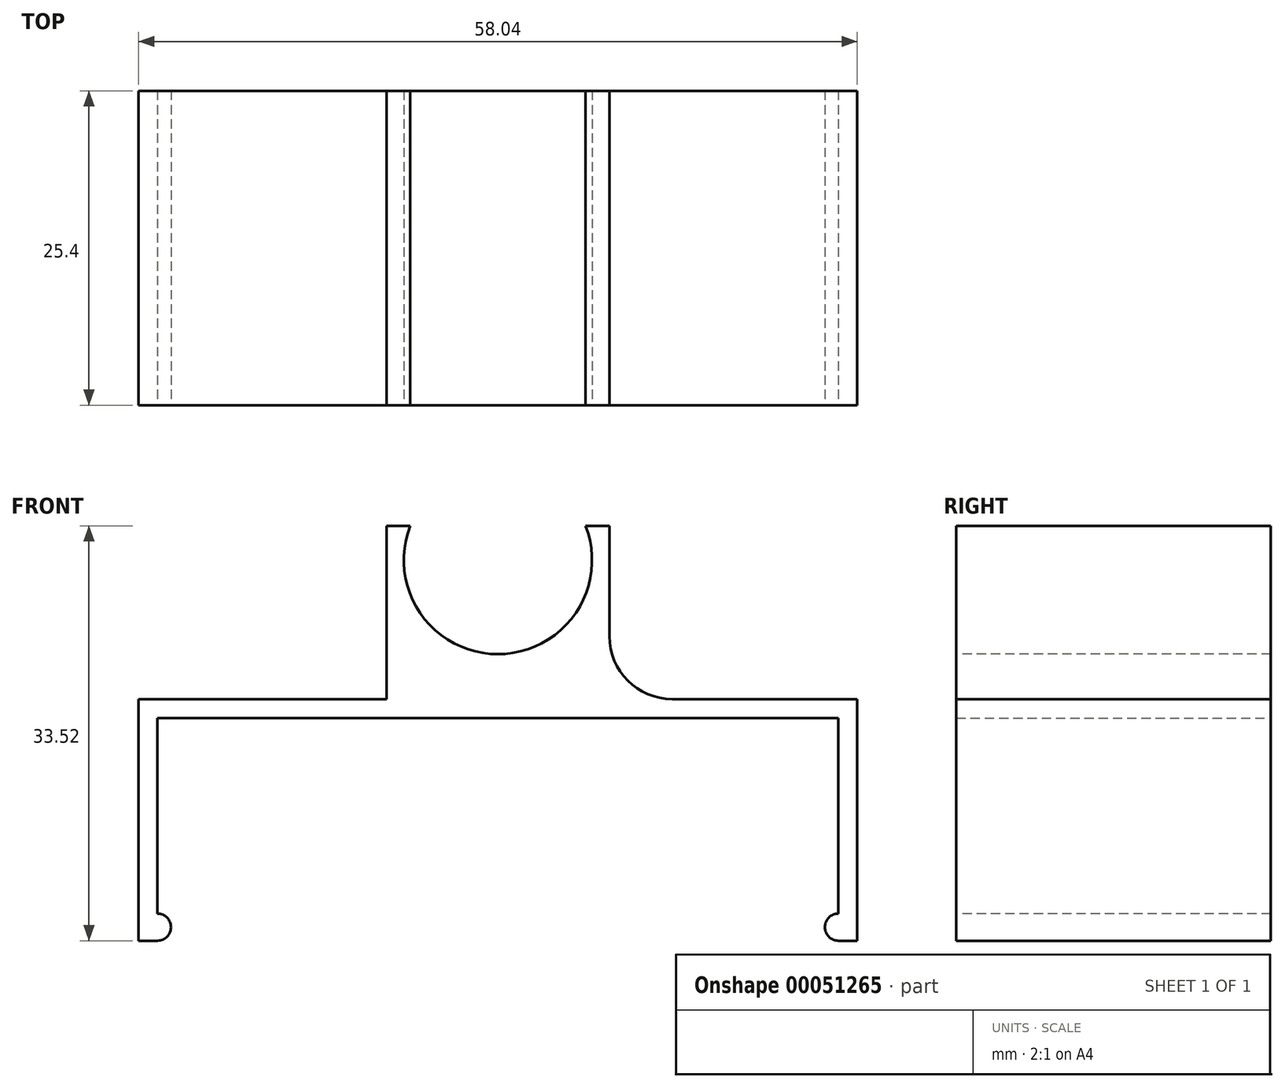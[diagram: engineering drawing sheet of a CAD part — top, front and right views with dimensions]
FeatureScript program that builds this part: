
annotation { "Feature Type Name" : "Feature", "Feature Type Description" : "" }
export const myFeature = defineFeature(function(context is Context, id is Id, definition is map)
    precondition{}
    {
        {
            var Q0;
            Q0=qCreatedBy(makeId("Front.planeOp"),FACE);
            var sketch = newSketch(context, id + "F0", { "sketchPlane" : qUnion([Q0])});
            skLineSegment(sketch, "E0", {"start": v(0, -30.9) * mm, "end": v(0, 35.03) * mm, "construction": true});
            skLineSegment(sketch, "E1", {"start": v(27.5, 0) * mm, "end": v(27.5, 18) * mm});
            skLineSegment(sketch, "E2", {"start": v(27.5, 18) * mm, "end": v(0, 18) * mm});
            skLineSegment(sketch, "E3.MirrorCS", {"start": v(-27.5, 18) * mm, "end": v(0, 18) * mm});
            skLineSegment(sketch, "E4.MirrorCS", {"start": v(-27.5, 0) * mm, "end": v(-27.5, 18) * mm});
            skLineSegment(sketch, "E5.0", {"start": v(29.02, 0) * mm, "end": v(29.02, 19.52) * mm});
            skLineSegment(sketch, "E5.1", {"start": v(29.02, 19.52) * mm, "end": v(0, 19.52) * mm});
            skLineSegment(sketch, "E5.2", {"start": v(-29.02, 19.52) * mm, "end": v(0, 19.52) * mm});
            skLineSegment(sketch, "E5.3", {"start": v(-29.02, 0) * mm, "end": v(-29.02, 19.52) * mm});
            skLineSegment(sketch, "E6", {"start": v(-29.02, 0) * mm, "end": v(-27.5, 0) * mm});
            skLineSegment(sketch, "E7", {"start": v(27.5, 0) * mm, "end": v(29.02, 0) * mm});
            skSolve(sketch);
        }
        {
            var Q0;
            Q0 = qSketchRegion(id + "F0", true);
            extrude(context, id + "F1", {"entities" : qUnion([Q0]), "endBound" : BoundingType.SYMMETRIC, "depth" : 25.4 * mm});
        }
        {
            var Q0;
            Q0=makeQuery(id+"F1.opExtrude","CAP_FACE",FACE,{"disambiguationData":[OSD([sQuery(id+"F0.wireOp",EDGE,"E1"),sQuery(id+"F0.wireOp",EDGE,"E2"),sQuery(id+"F0.wireOp",EDGE,"E3.MirrorCS"),sQuery(id+"F0.wireOp",EDGE,"E4.MirrorCS"),sQuery(id+"F0.wireOp",EDGE,"E5.0"),sQuery(id+"F0.wireOp",EDGE,"E5.1"),sQuery(id+"F0.wireOp",EDGE,"E5.2"),sQuery(id+"F0.wireOp",EDGE,"E5.3"),sQuery(id+"F0.wireOp",EDGE,"E6"),sQuery(id+"F0.wireOp",EDGE,"E7")])],"isStart":false});
            var sketch = newSketch(context, id + "F2", { "sketchPlane" : qUnion([Q0])});
            skArc(sketch, "E8", {"start": v(-27.5, 0) * mm, "mid": v(-26.4, 1.1) * mm, "end": v(-27.5, 2.2) * mm});
            skLineSegment(sketch, "E9", {"start": v(-27.5, 2.2) * mm, "end": v(-27.5, 0) * mm});
            skSolve(sketch);
        }
        {
            var Q0;
            Q0=makeQuery(id+"F2.imprint","IMPRINT",FACE,{"disambiguationData":[TD([[makeQuery(id+"F2.imprint","IMPRINT",EDGE,{"derivedFrom":sQuery(id+"F2.wireOp",EDGE,"E8")}),1.0]])]});
            var Q1;
            Q1=makeQuery(id+"F1.opExtrude","CAP_FACE",FACE,{"disambiguationData":[OSD([sQuery(id+"F0.wireOp",EDGE,"E1"),sQuery(id+"F0.wireOp",EDGE,"E2"),sQuery(id+"F0.wireOp",EDGE,"E3.MirrorCS"),sQuery(id+"F0.wireOp",EDGE,"E4.MirrorCS"),sQuery(id+"F0.wireOp",EDGE,"E5.0"),sQuery(id+"F0.wireOp",EDGE,"E5.1"),sQuery(id+"F0.wireOp",EDGE,"E5.2"),sQuery(id+"F0.wireOp",EDGE,"E5.3"),sQuery(id+"F0.wireOp",EDGE,"E6"),sQuery(id+"F0.wireOp",EDGE,"E7")])],"isStart":true});
            extrude(context, id + "F3", {"entities" : qUnion([Q0]), "endBound" : BoundingType.UP_TO_SURFACE, "oppositeDirection" : true, "endBoundEntityFace" : qUnion([Q1]), "depth" : 25.4 * mm});
        }
        {
            var Q0;
            Q0=makeQuery(id+"F3.opExtrude","SWEPT_BODY",BODY,{"disambiguationData":[OSD([sQuery(id+"F2.wireOp",EDGE,"E8"),sQuery(id+"F2.wireOp",EDGE,"E9")])]});
            var Q1;
            Q1=qCreatedBy(makeId("Right.planeOp"),FACE);
            mirror(context, id + "F4", {"operationType" : NewBodyOperationType.ADD, "entities" : qUnion([Q0]), "mirrorPlane" : qUnion([Q1])});
        }
        {
            var Q0;
            Q0=makeQuery(id+"F1.opExtrude","SWEPT_FACE",FACE,{"disambiguationData":[OSD([sQuery(id+"F0.wireOp",EDGE,"E5.1"),sQuery(id+"F0.wireOp",EDGE,"E5.2")])]});
            var sketch = newSketch(context, id + "F5", { "sketchPlane" : qUnion([Q0])});
            skLineSegment(sketch, "E10.rect.bottom", {"start": v(9, -12.7) * mm, "end": v(-9, -12.7) * mm});
            skLineSegment(sketch, "E10.rect.top", {"start": v(9, 12.7) * mm, "end": v(-9, 12.7) * mm});
            skLineSegment(sketch, "E10.rect.left", {"start": v(9, -12.7) * mm, "end": v(9, 12.7) * mm});
            skLineSegment(sketch, "E10.rect.right", {"start": v(-9, -12.7) * mm, "end": v(-9, 12.7) * mm});
            skPoint(sketch, "E10.rect.middle", {"position": v(0, 0) * mm});
            skSolve(sketch);
        }
        {
            var Q0;
            Q0=makeQuery(id+"F5.imprint","IMPRINT",FACE,{"disambiguationData":[TD([[makeQuery(id+"F5.imprint","IMPRINT",EDGE,{"derivedFrom":sQuery(id+"F5.wireOp",EDGE,"E10.rect.bottom")}),-1.0]])]});
            extrude(context, id + "F6", {"entities" : qUnion([Q0]), "operationType" : NewBodyOperationType.ADD, "depth" : 14 * mm});
        }
        {
            var Q0;
            {var subQ0=makeQuery(id+"F3.opExtrude","CAP_FACE",FACE,{"disambiguationData":[OSD([sQuery(id+"F2.wireOp",EDGE,"E8"),sQuery(id+"F2.wireOp",EDGE,"E9")])],"isStart":true});Q0=makeQuery(id+"F6.boolean.opBoolean","MERGE",FACE,{"derivedFrom":[makeQuery(id+"F4.boolean.opBoolean","MERGE",FACE,{"derivedFrom":[makeQuery(id+"F1.opExtrude","CAP_FACE",FACE,{"disambiguationData":[OSD([sQuery(id+"F0.wireOp",EDGE,"E1"),sQuery(id+"F0.wireOp",EDGE,"E2"),sQuery(id+"F0.wireOp",EDGE,"E3.MirrorCS"),sQuery(id+"F0.wireOp",EDGE,"E4.MirrorCS"),sQuery(id+"F0.wireOp",EDGE,"E5.0"),sQuery(id+"F0.wireOp",EDGE,"E5.1"),sQuery(id+"F0.wireOp",EDGE,"E5.2"),sQuery(id+"F0.wireOp",EDGE,"E5.3"),sQuery(id+"F0.wireOp",EDGE,"E6"),sQuery(id+"F0.wireOp",EDGE,"E7")])],"isStart":false}),subQ0,makeQuery(id+"F4.opPattern","COPY",FACE,{"derivedFrom":subQ0,"instanceName":"1"})]}),makeQuery(id+"F6.opExtrude","SWEPT_FACE",FACE,{"disambiguationData":[OSD([sQuery(id+"F5.wireOp",EDGE,"E10.rect.bottom")])]})]});}
            var sketch = newSketch(context, id + "F7", { "sketchPlane" : qUnion([Q0])});
            skCircle(sketch, "E11", {"center": v(0, 30.75) * mm, "radius": 7.6 * mm});
            skPoint(sketch, "E12", {"position": v(0, 33.52) * mm});
            skSolve(sketch);
        }
        {
            var Q0;
            {var subQ0=sQuery(id+"F7.wireOp",EDGE,"E11");var subQ1=makeQuery(id+"F6.opExtrude","CAP_EDGE",EDGE,{"disambiguationData":[OSD([sQuery(id+"F5.wireOp",EDGE,"E10.rect.bottom")])],"isStart":false});var subQ2=makeQuery(id+"F7.imprint","INTERSECT",VERTEX,{"disambiguationData":[OD(0.0)],"derivedFrom":[subQ1,subQ0]});Q0=makeQuery(id+"F7.imprint","IMPRINT",FACE,{"disambiguationData":[TD([[makeQuery(id+"F7.imprint","IMPRINT",EDGE,{"disambiguationData":[TD([[subQ2,1.0]])],"derivedFrom":subQ0}),1.0]])]});}
            extrude(context, id + "F8", {"entities" : qUnion([Q0]), "operationType" : NewBodyOperationType.REMOVE, "endBound" : BoundingType.THROUGH_ALL, "oppositeDirection" : true, "depth" : 25.4 * mm});
        }
        {
            var Q0;
            Q0=makeQuery(id+"F6.opExtrude","CAP_EDGE",EDGE,{"disambiguationData":[OSD([sQuery(id+"F5.wireOp",EDGE,"E10.rect.left")])],"isStart":true});
            var Q1;
            Q1=makeQuery(id+"F6.opExtrude","CAP_EDGE",EDGE,{"disambiguationData":[OSD([sQuery(id+"F5.wireOp",EDGE,"E10.rect.right")])],"isStart":true});
            fillet(context, id + "F9", {"entities" : qUnion([Q0, Q1]), "radius" : 5.08 * mm, "tangentPropagation" : true, "allowEdgeOverflow" : false});
        }
    });
